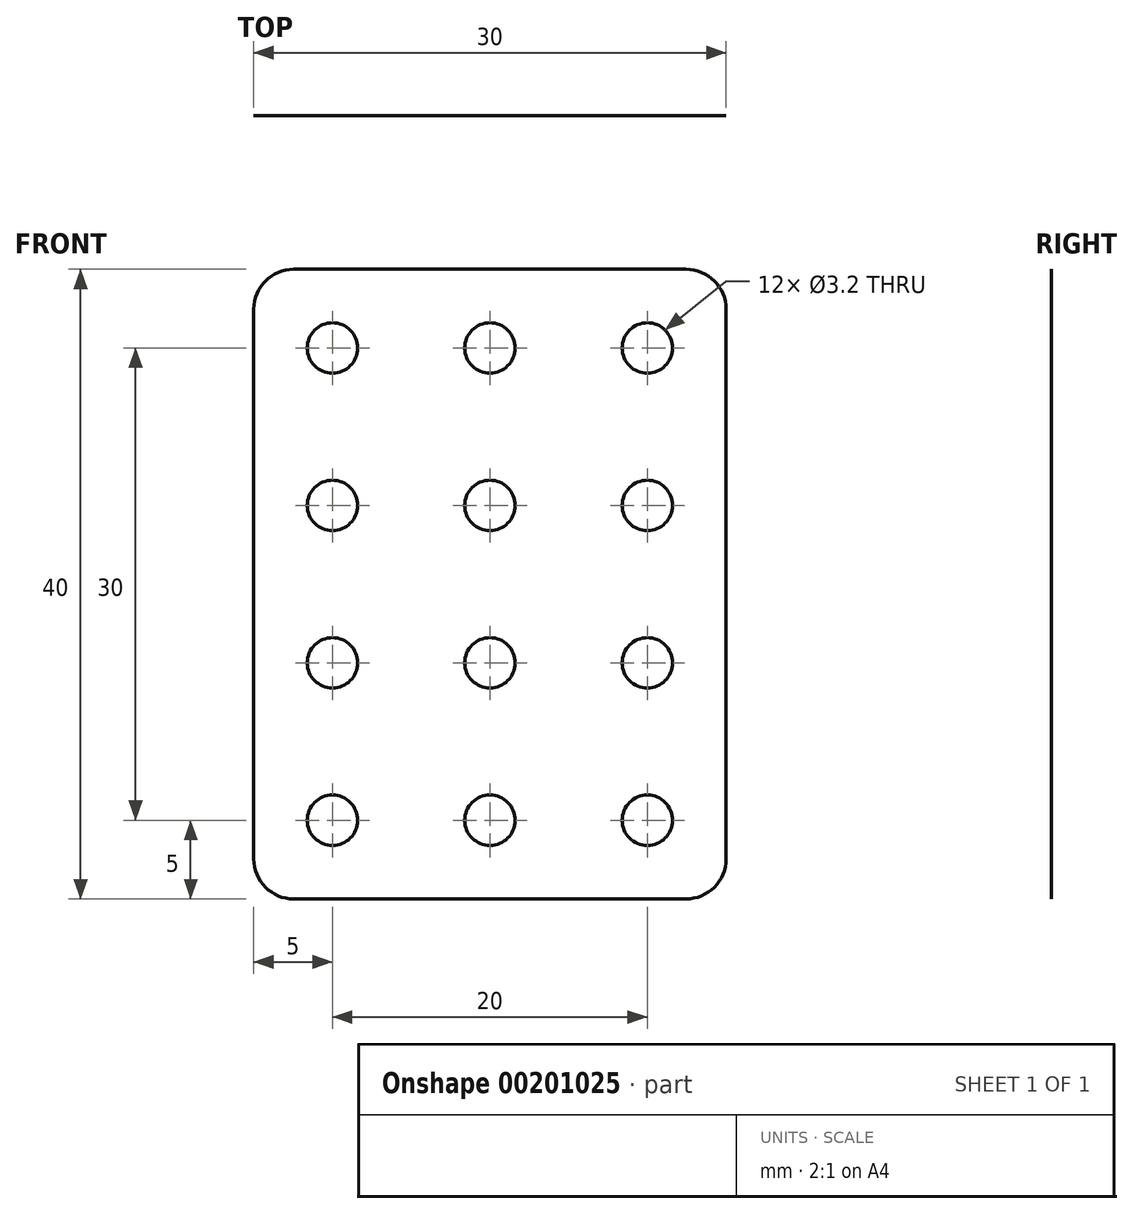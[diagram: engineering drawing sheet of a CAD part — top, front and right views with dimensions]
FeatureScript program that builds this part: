
annotation { "Feature Type Name" : "Feature", "Feature Type Description" : "" }
export const myFeature = defineFeature(function(context is Context, id is Id, definition is map)
    precondition{}
    {
        {
            var Q0;
            Q0=qCreatedBy(makeId("Front.planeOp"),FACE);
            var sketch = newSketch(context, id + "F0", { "sketchPlane" : qUnion([Q0])});
            skLineSegment(sketch, "E0.bottom", {"start": v(2.54, 0) * mm, "end": v(27.46, 0) * mm});
            skLineSegment(sketch, "E0.top", {"start": v(2.54, -40) * mm, "end": v(27.46, -40) * mm});
            skLineSegment(sketch, "E0.left", {"start": v(0, -2.54) * mm, "end": v(0, -37.46) * mm});
            skLineSegment(sketch, "E0.right", {"start": v(30, -2.54) * mm, "end": v(30, -37.46) * mm});
            skPoint(sketch, "E1.visualSharp", {"position": v(0, 0) * mm});
            skArc(sketch, "E1.filletArc", {"start": v(2.54, 0) * mm, "mid": v(0.74, -0.74) * mm, "end": v(0, -2.54) * mm});
            skPoint(sketch, "E2.visualSharp", {"position": v(30, 0) * mm});
            skArc(sketch, "E2.filletArc", {"start": v(30, -2.54) * mm, "mid": v(29.26, -0.74) * mm, "end": v(27.46, 0) * mm});
            skPoint(sketch, "E3.visualSharp", {"position": v(30, -40) * mm});
            skArc(sketch, "E3.filletArc", {"start": v(27.46, -40) * mm, "mid": v(29.26, -39.26) * mm, "end": v(30, -37.46) * mm});
            skPoint(sketch, "E4.visualSharp", {"position": v(0, -40) * mm});
            skArc(sketch, "E4.filletArc", {"start": v(0, -37.46) * mm, "mid": v(0.74, -39.26) * mm, "end": v(2.54, -40) * mm});
            skCircle(sketch, "E5", {"center": v(5, -5) * mm, "radius": 1.6 * mm});
            skCircle(sketch, "E6.0.1.0", {"center": v(5, -15) * mm, "radius": 1.6 * mm});
            skCircle(sketch, "E6.0.2.0", {"center": v(5, -25) * mm, "radius": 1.6 * mm});
            skCircle(sketch, "E6.0.3.0", {"center": v(5, -35) * mm, "radius": 1.6 * mm});
            skCircle(sketch, "E6.1.0.0", {"center": v(15, -5) * mm, "radius": 1.6 * mm});
            skCircle(sketch, "E6.1.1.0", {"center": v(15, -15) * mm, "radius": 1.6 * mm});
            skCircle(sketch, "E6.1.2.0", {"center": v(15, -25) * mm, "radius": 1.6 * mm});
            skCircle(sketch, "E6.1.3.0", {"center": v(15, -35) * mm, "radius": 1.6 * mm});
            skCircle(sketch, "E6.2.0.0", {"center": v(25, -5) * mm, "radius": 1.6 * mm});
            skCircle(sketch, "E6.2.1.0", {"center": v(25, -15) * mm, "radius": 1.6 * mm});
            skCircle(sketch, "E6.2.2.0", {"center": v(25, -25) * mm, "radius": 1.6 * mm});
            skCircle(sketch, "E6.2.3.0", {"center": v(25, -35) * mm, "radius": 1.6 * mm});
            skLineSegment(sketch, "E6.direction1", {"start": v(5, -5) * mm, "end": v(15, -5) * mm, "construction": true});
            skLineSegment(sketch, "E6.direction2", {"start": v(5, -5) * mm, "end": v(5, -15) * mm, "construction": true});
            skSolve(sketch);
        }
        {
            var Q0;
            Q0=makeQuery(id+"F0.imprint","IMPRINT",FACE,{"disambiguationData":[TD([[makeQuery(id+"F0.imprint","IMPRINT",EDGE,{"derivedFrom":sQuery(id+"F0.wireOp",EDGE,"E0.bottom")}),-1.0]])]});
            extrude(context, id + "F1", {"entities" : qUnion([Q0]), "depth" : 1 / 203.2 * mm});
        }
    });
